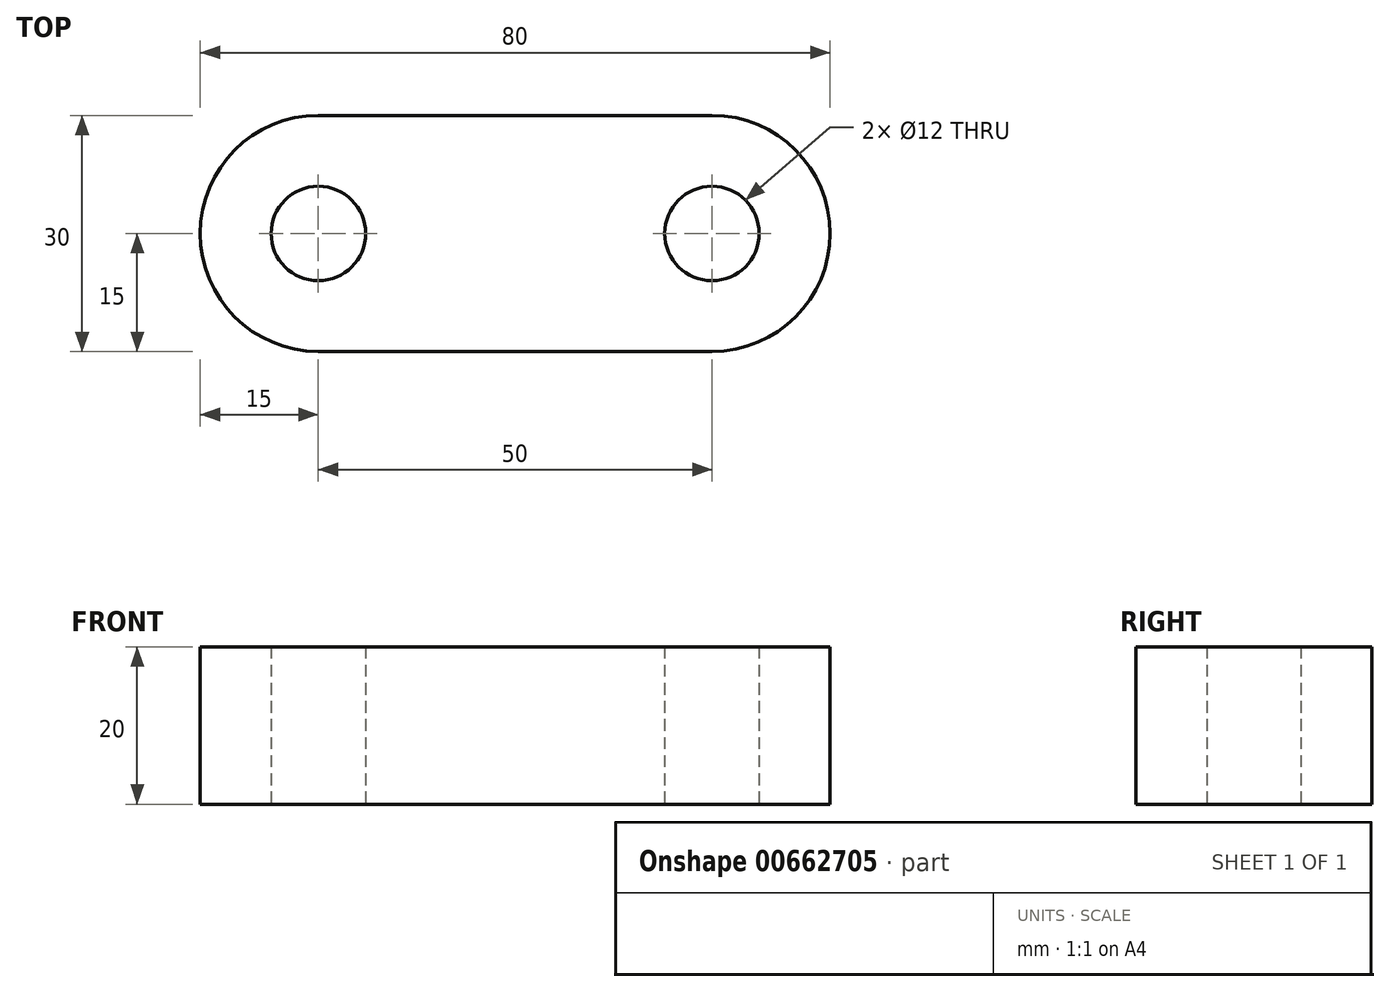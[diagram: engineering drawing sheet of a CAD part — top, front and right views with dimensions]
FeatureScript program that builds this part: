
annotation { "Feature Type Name" : "Feature", "Feature Type Description" : "" }
export const myFeature = defineFeature(function(context is Context, id is Id, definition is map)
    precondition{}
    {
        {
            var Q0;
            Q0=qCreatedBy(makeId("Top.planeOp"),FACE);
            var sketch = newSketch(context, id + "F0", { "sketchPlane" : qUnion([Q0])});
            skLineSegment(sketch, "E0", {"start": v(-25, 15) * mm, "end": v(25, 15) * mm});
            skLineSegment(sketch, "E1", {"start": v(-25, -15) * mm, "end": v(25, -15) * mm});
            skArc(sketch, "E2", {"start": v(-25, 15) * mm, "mid": v(-40, 0) * mm, "end": v(-25, -15) * mm});
            skArc(sketch, "E3", {"start": v(25, -15) * mm, "mid": v(40, 0) * mm, "end": v(25, 15) * mm});
            skCircle(sketch, "E4", {"center": v(-25, 0) * mm, "radius": 6 * mm});
            skCircle(sketch, "E5", {"center": v(25, 0) * mm, "radius": 6 * mm});
            skSolve(sketch);
        }
        {
            var Q0;
            Q0=makeQuery(id+"F0.imprint","IMPRINT",FACE,{"disambiguationData":[TD([[makeQuery(id+"F0.imprint","IMPRINT",EDGE,{"derivedFrom":sQuery(id+"F0.wireOp",EDGE,"E0")}),-1.0]])]});
            extrude(context, id + "F1", {"entities" : qUnion([Q0]), "depth" : 20 * mm, "offsetDistance" : 25 * mm});
        }
    });
